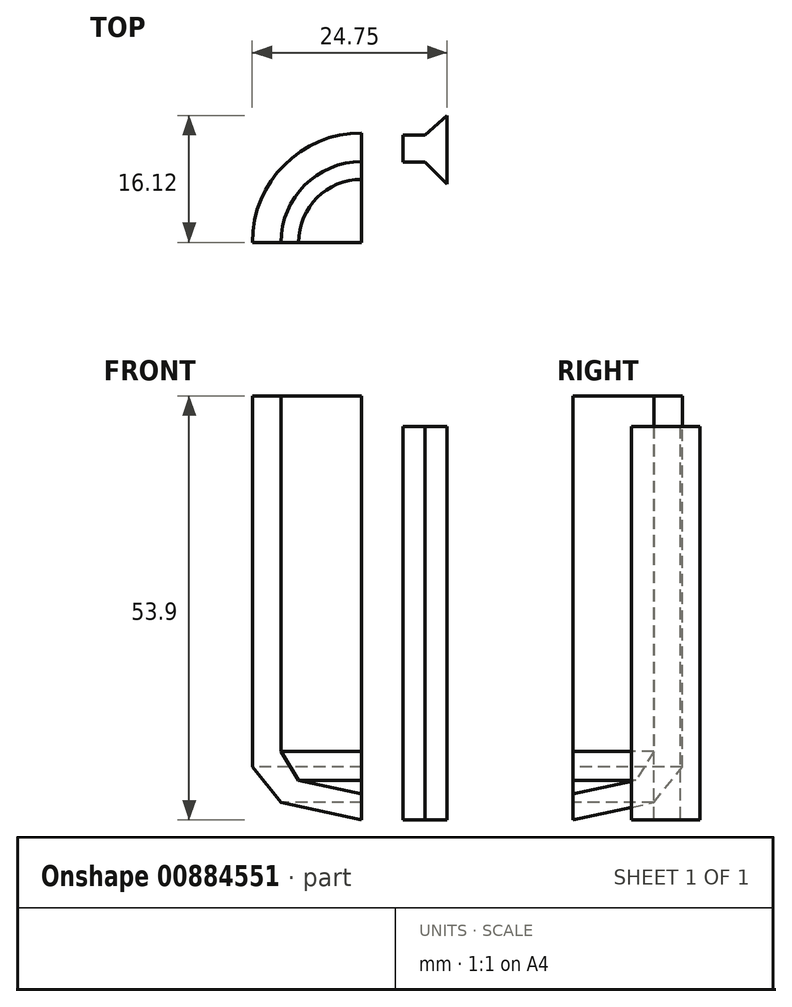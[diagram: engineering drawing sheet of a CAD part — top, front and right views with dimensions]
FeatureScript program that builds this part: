
annotation { "Feature Type Name" : "Feature", "Feature Type Description" : "" }
export const myFeature = defineFeature(function(context is Context, id is Id, definition is map)
    precondition{}
    {
        {
            var Q0;
            Q0=qCreatedBy(makeId("Front.planeOp"),FACE);
            var sketch = newSketch(context, id + "F0", { "sketchPlane" : qUnion([Q0])});
            skLineSegment(sketch, "E0", {"start": v(0, 0) * mm, "end": v(-10.25, 2.25) * mm});
            skLineSegment(sketch, "E1", {"start": v(-10.25, 2.25) * mm, "end": v(-13.9, 6.74) * mm});
            skLineSegment(sketch, "E2", {"start": v(-13.9, 6.74) * mm, "end": v(-13.9, 53.9) * mm});
            skLineSegment(sketch, "E3", {"start": v(-13.9, 53.9) * mm, "end": v(-10.25, 53.9) * mm});
            skLineSegment(sketch, "E4", {"start": v(-10.25, 53.9) * mm, "end": v(-10.25, 8.7) * mm});
            skLineSegment(sketch, "E5", {"start": v(-10.25, 8.7) * mm, "end": v(-8, 5.05) * mm});
            skLineSegment(sketch, "E6", {"start": v(-8, 5.05) * mm, "end": v(0, 3.3) * mm});
            skLineSegment(sketch, "E7", {"start": v(0, 3.3) * mm, "end": v(0, 0) * mm});
            skSolve(sketch);
        }
        {
            var Q0;
            Q0=makeQuery(id+"F0.imprint","IMPRINT",FACE,{"disambiguationData":[TD([[makeQuery(id+"F0.imprint","IMPRINT",EDGE,{"derivedFrom":sQuery(id+"F0.wireOp",EDGE,"E0")}),-1.0]])]});
            var Q1;
            Q1=sQuery(id+"F0.wireOp",EDGE,"E7");
            revolve(context, id + "F1", {"surfaceOperationType" : NewSurfaceOperationType.NEW, "entities" : qUnion([Q0]), "axis" : qUnion([Q1]), "revolveType" : RevolveType.ONE_DIRECTION, "angle" : 90 * degree});
        }
        {
            var Q0;
            Q0=qCreatedBy(makeId("Top.planeOp"),FACE);
            var sketch = newSketch(context, id + "F2", { "sketchPlane" : qUnion([Q0])});
            skLineSegment(sketch, "E8", {"start": v(5.24, 13.6) * mm, "end": v(5.24, 10.22) * mm});
            skLineSegment(sketch, "E9", {"start": v(5.24, 10.22) * mm, "end": v(8.05, 10.22) * mm});
            skLineSegment(sketch, "E10", {"start": v(8.05, 10.22) * mm, "end": v(10.85, 7.41) * mm});
            skLineSegment(sketch, "E11", {"start": v(10.85, 7.41) * mm, "end": v(10.85, 16.12) * mm});
            skLineSegment(sketch, "E12", {"start": v(10.85, 16.12) * mm, "end": v(8.05, 13.6) * mm});
            skLineSegment(sketch, "E13", {"start": v(8.05, 13.6) * mm, "end": v(5.24, 13.6) * mm});
            skSolve(sketch);
        }
        {
            var Q0;
            Q0=makeQuery(id+"F2.imprint","IMPRINT",FACE,{"disambiguationData":[TD([[makeQuery(id+"F2.imprint","IMPRINT",EDGE,{"derivedFrom":sQuery(id+"F2.wireOp",EDGE,"E8")}),1.0]])]});
            extrude(context, id + "F3", {"entities" : qUnion([Q0]), "depth" : 50 * mm, "offsetDistance" : 25 * mm});
        }
    });
